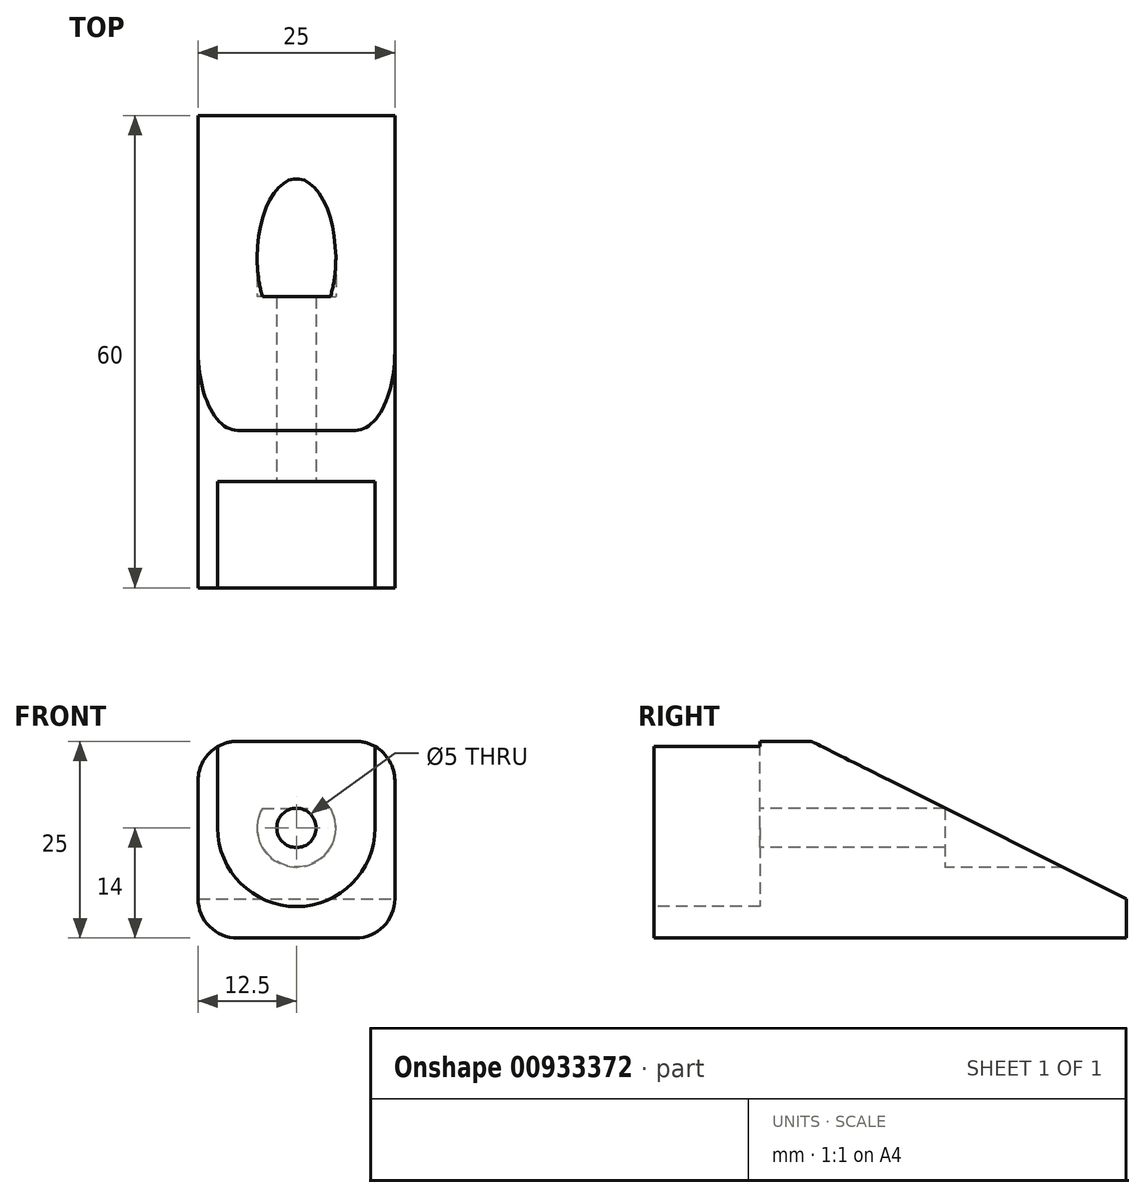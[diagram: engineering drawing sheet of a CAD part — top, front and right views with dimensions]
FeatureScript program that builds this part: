
annotation { "Feature Type Name" : "Feature", "Feature Type Description" : "" }
export const myFeature = defineFeature(function(context is Context, id is Id, definition is map)
    precondition{}
    {
        {
            var Q0;
            Q0=qCreatedBy(makeId("Top.planeOp"),FACE);
            var sketch = newSketch(context, id + "F0", { "sketchPlane" : qUnion([Q0])});
            skLineSegment(sketch, "E0.bottom", {"start": v(12.5, -30) * mm, "end": v(-12.5, -30) * mm});
            skLineSegment(sketch, "E0.top", {"start": v(12.5, 30) * mm, "end": v(-12.5, 30) * mm});
            skLineSegment(sketch, "E0.left", {"start": v(12.5, -30) * mm, "end": v(12.5, 30) * mm});
            skLineSegment(sketch, "E0.right", {"start": v(-12.5, -30) * mm, "end": v(-12.5, 30) * mm});
            skPoint(sketch, "E0.middle", {"position": v(0, 0) * mm});
            skSolve(sketch);
        }
        {
            var Q0;
            Q0 = qSketchRegion(id + "F0", true);
            extrude(context, id + "F1", {"entities" : qUnion([Q0]), "depth" : 25 * mm, "offsetDistance" : 25 * mm});
        }
        {
            var Q0;
            Q0=makeQuery(id+"F1.opExtrude","CAP_EDGE",EDGE,{"disambiguationData":[OSD([sQuery(id+"F0.wireOp",EDGE,"E0.left")])],"isStart":false});
            var Q1;
            Q1=makeQuery(id+"F1.opExtrude","CAP_EDGE",EDGE,{"disambiguationData":[OSD([sQuery(id+"F0.wireOp",EDGE,"E0.left")])],"isStart":true});
            var Q2;
            Q2=makeQuery(id+"F1.opExtrude","CAP_EDGE",EDGE,{"disambiguationData":[OSD([sQuery(id+"F0.wireOp",EDGE,"E0.right")])],"isStart":true});
            var Q3;
            Q3=makeQuery(id+"F1.opExtrude","CAP_EDGE",EDGE,{"disambiguationData":[OSD([sQuery(id+"F0.wireOp",EDGE,"E0.right")])],"isStart":false});
            fillet(context, id + "F2", {"entities" : qUnion([Q0, Q1, Q2, Q3]), "radius" : 5 * mm, "tangentPropagation" : true, "allowEdgeOverflow" : false});
        }
        {
            var Q0;
            Q0=makeQuery(id+"F1.opExtrude","SWEPT_FACE",FACE,{"disambiguationData":[OSD([sQuery(id+"F0.wireOp",EDGE,"E0.bottom")])]});
            var sketch = newSketch(context, id + "F3", { "sketchPlane" : qUnion([Q0])});
            skCircle(sketch, "E1", {"center": v(0, 14) * mm, "radius": 10 * mm});
            skLineSegment(sketch, "E2.bottom", {"start": v(10, 14) * mm, "end": v(-10, 14) * mm});
            skLineSegment(sketch, "E2.top", {"start": v(10, 36) * mm, "end": v(-10, 36) * mm});
            skLineSegment(sketch, "E2.left", {"start": v(10, 14) * mm, "end": v(10, 36) * mm});
            skLineSegment(sketch, "E2.right", {"start": v(-10, 14) * mm, "end": v(-10, 36) * mm});
            skPoint(sketch, "E2.middle", {"position": v(0, 25) * mm});
            skSolve(sketch);
        }
        {
            var Q0;
            Q0=makeQuery(id+"F3.imprint","IMPRINT",FACE,{"disambiguationData":[TD([[makeQuery(id+"F3.imprint","IMPRINT",EDGE,{"derivedFrom":sQuery(id+"F3.wireOp",EDGE,"E1")}),1.0]])]});
            extrude(context, id + "F4", {"entities" : qUnion([Q0]), "operationType" : NewBodyOperationType.REMOVE, "oppositeDirection" : true, "depth" : 13.5 * mm, "offsetDistance" : 25 * mm});
        }
        {
            var Q0;
            {var subQ4=sQuery(id+"F0.wireOp",EDGE,"E0.bottom");var subQ8=makeQuery(id+"F1.opExtrude","CAP_EDGE",EDGE,{"disambiguationData":[OSD([subQ4])],"isStart":false});Q0=makeQuery(id+"F3.imprint","IMPRINT",FACE,{"disambiguationData":[TD([[makeQuery(id+"F3.imprint","IMPRINT",EDGE,{"derivedFrom":subQ8}),1.0]])]});}
            extrude(context, id + "F5", {"entities" : qUnion([Q0]), "operationType" : NewBodyOperationType.REMOVE, "oppositeDirection" : true, "depth" : 13.5 * mm, "offsetDistance" : 25 * mm});
        }
        {
            var Q0;
            Q0=makeQuery(id+"F1.opExtrude","CAP_EDGE",EDGE,{"disambiguationData":[OSD([sQuery(id+"F0.wireOp",EDGE,"E0.top")])],"isStart":false});
            chamfer(context, id + "F6", {"entities" : qUnion([Q0]), "chamferType" : ChamferType.TWO_OFFSETS, "width1" : 40 * mm, "oppositeDirection" : false, "width2" : 20 * mm});
        }
        {
            var Q0;
            {var subQ0=sQuery(id+"F3.wireOp",EDGE,"E1");Q0=makeQuery(id+"F5.boolean.opBoolean","MERGE",FACE,{"derivedFrom":[makeQuery(id+"F4.boolean.opBoolean","COPY",FACE,{"derivedFrom":makeQuery(id+"F4.opExtrude","CAP_FACE",FACE,{"disambiguationData":[OSD([subQ0])],"isStart":false})})],"fromTools":[makeQuery(id+"F5.opExtrude","CAP_FACE",FACE,{"disambiguationData":[OSD([sQuery(id+"F0.wireOp",EDGE,"E0.bottom"),sQuery(id+"F0.wireOp",EDGE,"E0.left"),sQuery(id+"F0.wireOp",EDGE,"E0.right"),subQ0,sQuery(id+"F3.wireOp",EDGE,"E2.left"),sQuery(id+"F3.wireOp",EDGE,"E2.right")])],"isStart":false})]});}
            var sketch = newSketch(context, id + "F7", { "sketchPlane" : qUnion([Q0])});
            skCircle(sketch, "E3", {"center": v(0, 14) * mm, "radius": 2.5 * mm});
            skSolve(sketch);
        }
        {
            var Q0;
            Q0 = qSketchRegion(id + "F7", true);
            extrude(context, id + "F8", {"entities" : qUnion([Q0]), "operationType" : NewBodyOperationType.REMOVE, "oppositeDirection" : true, "depth" : 55 * mm, "offsetDistance" : 25 * mm});
        }
        {
            var Q0;
            {var subQ0=sQuery(id+"F3.wireOp",EDGE,"E1");Q0=makeQuery(id+"F5.boolean.opBoolean","MERGE",FACE,{"derivedFrom":[makeQuery(id+"F4.boolean.opBoolean","COPY",FACE,{"derivedFrom":makeQuery(id+"F4.opExtrude","CAP_FACE",FACE,{"disambiguationData":[OSD([subQ0])],"isStart":false})})],"fromTools":[makeQuery(id+"F5.opExtrude","CAP_FACE",FACE,{"disambiguationData":[OSD([sQuery(id+"F0.wireOp",EDGE,"E0.bottom"),sQuery(id+"F0.wireOp",EDGE,"E0.left"),sQuery(id+"F0.wireOp",EDGE,"E0.right"),subQ0,sQuery(id+"F3.wireOp",EDGE,"E2.left"),sQuery(id+"F3.wireOp",EDGE,"E2.right")])],"isStart":false})]});}
            var sketch = newSketch(context, id + "F9", { "sketchPlane" : qUnion([Q0])});
            skCircle(sketch, "E4", {"center": v(0, 14) * mm, "radius": 5 * mm});
            skSolve(sketch);
        }
        {
            var Q0;
            Q0 = qSketchRegion(id + "F9", true);
            extrude(context, id + "F10", {"entities" : qUnion([Q0]), "operationType" : NewBodyOperationType.REMOVE, "oppositeDirection" : true, "depth" : 46.5 * mm, "offsetDistance" : 25 * mm, "hasSecondDirection" : true, "secondDirectionOppositeDirection" : true, "secondDirectionDepth" : 23.5 * mm});
        }
    });
